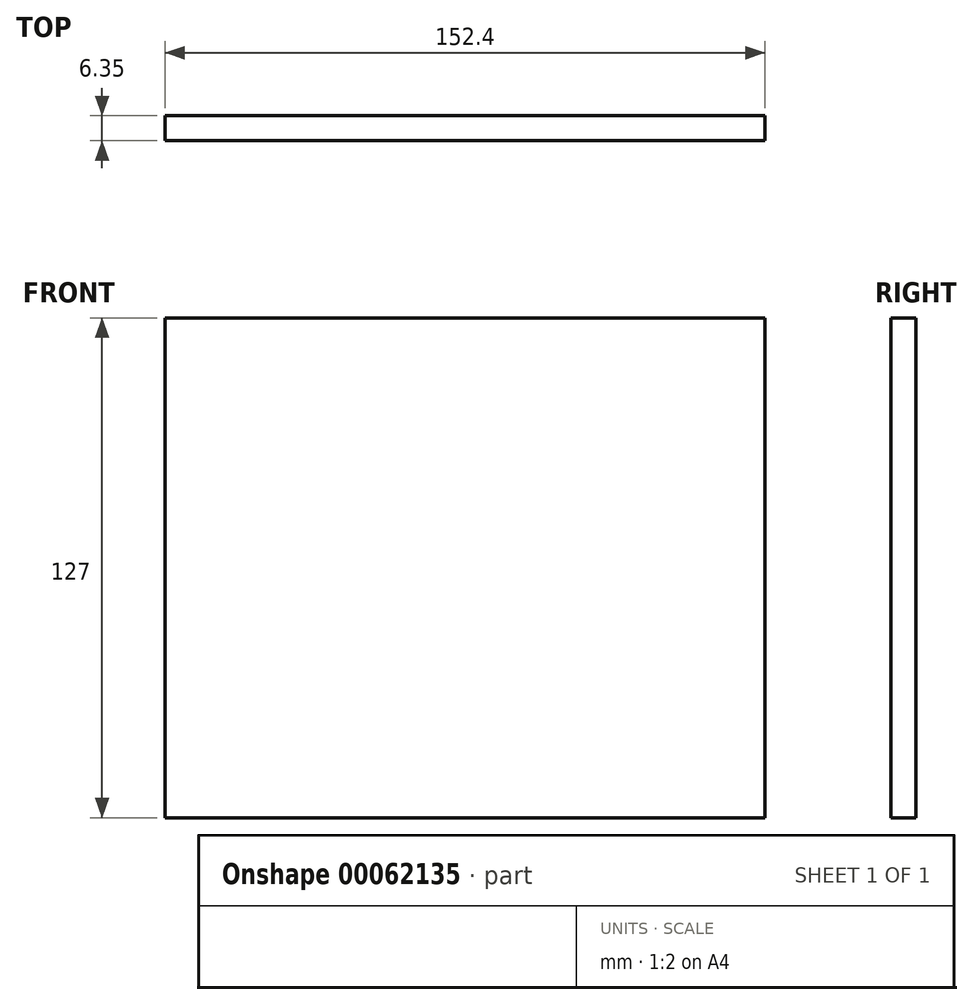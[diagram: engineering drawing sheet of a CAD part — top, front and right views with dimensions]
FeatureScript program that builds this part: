
annotation { "Feature Type Name" : "Feature", "Feature Type Description" : "" }
export const myFeature = defineFeature(function(context is Context, id is Id, definition is map)
    precondition{}
    {
        {
            var Q0;
            Q0=qCreatedBy(makeId("Front.planeOp"),FACE);
            var sketch = newSketch(context, id + "F0", { "sketchPlane" : qUnion([Q0])});
            skLineSegment(sketch, "E0.rect.bottom", {"start": v(76.2, 63.5) * mm, "end": v(-76.2, 63.5) * mm});
            skLineSegment(sketch, "E0.rect.top", {"start": v(76.2, -63.5) * mm, "end": v(-76.2, -63.5) * mm});
            skLineSegment(sketch, "E0.rect.left", {"start": v(76.2, 63.5) * mm, "end": v(76.2, -63.5) * mm});
            skLineSegment(sketch, "E0.rect.right", {"start": v(-76.2, 63.5) * mm, "end": v(-76.2, -63.5) * mm});
            skPoint(sketch, "E0.rect.middle", {"position": v(0, 0) * mm});
            skSolve(sketch);
        }
        {
            var Q0;
            Q0 = qSketchRegion(id + "F0", true);
            extrude(context, id + "F1", {"entities" : qUnion([Q0]), "depth" : 6.35 * mm, "offsetDistance" : 25.4 * mm});
        }
    });
